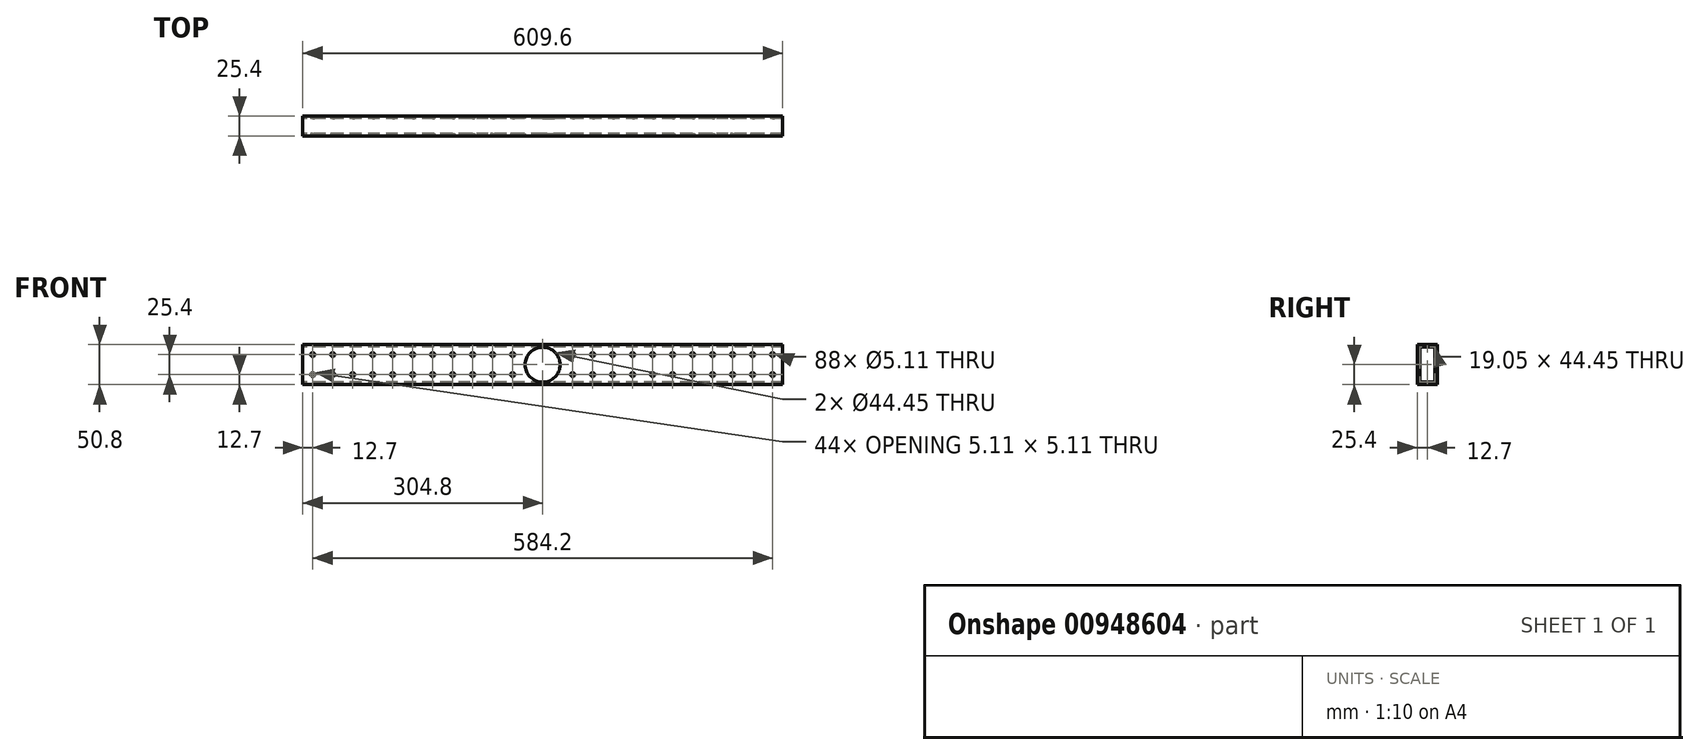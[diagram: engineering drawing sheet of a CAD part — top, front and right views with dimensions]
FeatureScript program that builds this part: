
annotation { "Feature Type Name" : "Feature", "Feature Type Description" : "" }
export const myFeature = defineFeature(function(context is Context, id is Id, definition is map)
    precondition{}
    {
        {
            var Q0;
            Q0=qCreatedBy(makeId("Right.planeOp"),FACE);
            var sketch = newSketch(context, id + "F0", { "sketchPlane" : qUnion([Q0])});
            skLineSegment(sketch, "E0.bottom", {"start": v(12.7, 25.4) * mm, "end": v(-12.7, 25.4) * mm});
            skLineSegment(sketch, "E0.top", {"start": v(12.7, -25.4) * mm, "end": v(-12.7, -25.4) * mm});
            skLineSegment(sketch, "E0.left", {"start": v(12.7, 25.4) * mm, "end": v(12.7, -25.4) * mm});
            skLineSegment(sketch, "E0.right", {"start": v(-12.7, 25.4) * mm, "end": v(-12.7, -25.4) * mm});
            skPoint(sketch, "E0.middle", {"position": v(0, 0) * mm});
            skLineSegment(sketch, "E1.0", {"start": v(9.53, 22.22) * mm, "end": v(-9.52, 22.22) * mm});
            skLineSegment(sketch, "E1.1", {"start": v(9.53, 22.22) * mm, "end": v(9.53, -22.23) * mm});
            skLineSegment(sketch, "E1.2", {"start": v(9.53, -22.23) * mm, "end": v(-9.52, -22.23) * mm});
            skLineSegment(sketch, "E1.3", {"start": v(-9.52, 22.22) * mm, "end": v(-9.53, -22.23) * mm});
            skSolve(sketch);
        }
        {
            var Q0;
            Q0 = qSketchRegion(id + "F0", true);
            extrude(context, id + "F1", {"entities" : qUnion([Q0]), "depth" : 609.6 * mm, "offsetDistance" : 25.4 * mm});
        }
        {
            var Q0;
            Q0=makeQuery(id+"F1.opExtrude","SWEPT_FACE",FACE,{"disambiguationData":[OSD([sQuery(id+"F0.wireOp",EDGE,"E0.right")])]});
            var sketch = newSketch(context, id + "F2", { "sketchPlane" : qUnion([Q0])});
            skCircle(sketch, "E2", {"center": v(12.7, 12.7) * mm, "radius": 2.55 * mm});
            skCircle(sketch, "E3.0.1.0", {"center": v(12.7, -12.7) * mm, "radius": 2.55 * mm});
            skCircle(sketch, "E3.1.0.0", {"center": v(38.1, 12.7) * mm, "radius": 2.55 * mm});
            skCircle(sketch, "E3.1.1.0", {"center": v(38.1, -12.7) * mm, "radius": 2.55 * mm});
            skCircle(sketch, "E3.2.0.0", {"center": v(63.5, 12.7) * mm, "radius": 2.55 * mm});
            skCircle(sketch, "E3.2.1.0", {"center": v(63.5, -12.7) * mm, "radius": 2.55 * mm});
            skCircle(sketch, "E3.3.0.0", {"center": v(88.9, 12.7) * mm, "radius": 2.55 * mm});
            skCircle(sketch, "E3.3.1.0", {"center": v(88.9, -12.7) * mm, "radius": 2.55 * mm});
            skCircle(sketch, "E3.4.0.0", {"center": v(114.3, 12.7) * mm, "radius": 2.55 * mm});
            skCircle(sketch, "E3.4.1.0", {"center": v(114.3, -12.7) * mm, "radius": 2.55 * mm});
            skCircle(sketch, "E3.5.0.0", {"center": v(139.7, 12.7) * mm, "radius": 2.55 * mm});
            skCircle(sketch, "E3.5.1.0", {"center": v(139.7, -12.7) * mm, "radius": 2.55 * mm});
            skCircle(sketch, "E3.6.0.0", {"center": v(165.1, 12.7) * mm, "radius": 2.55 * mm});
            skCircle(sketch, "E3.6.1.0", {"center": v(165.1, -12.7) * mm, "radius": 2.55 * mm});
            skCircle(sketch, "E3.7.0.0", {"center": v(190.5, 12.7) * mm, "radius": 2.55 * mm});
            skCircle(sketch, "E3.7.1.0", {"center": v(190.5, -12.7) * mm, "radius": 2.55 * mm});
            skCircle(sketch, "E3.8.0.0", {"center": v(215.9, 12.7) * mm, "radius": 2.55 * mm});
            skCircle(sketch, "E3.8.1.0", {"center": v(215.9, -12.7) * mm, "radius": 2.55 * mm});
            skCircle(sketch, "E3.9.0.0", {"center": v(241.3, 12.7) * mm, "radius": 2.55 * mm});
            skCircle(sketch, "E3.9.1.0", {"center": v(241.3, -12.7) * mm, "radius": 2.55 * mm});
            skCircle(sketch, "E3.10.0.0", {"center": v(266.7, 12.7) * mm, "radius": 2.55 * mm});
            skCircle(sketch, "E3.10.1.0", {"center": v(266.7, -12.7) * mm, "radius": 2.55 * mm});
            skCircle(sketch, "E3.11.0.0", {"center": v(292.1, 12.7) * mm, "radius": 2.55 * mm});
            skCircle(sketch, "E3.11.1.0", {"center": v(292.1, -12.7) * mm, "radius": 2.55 * mm});
            skCircle(sketch, "E3.12.0.0", {"center": v(317.5, 12.7) * mm, "radius": 2.55 * mm});
            skCircle(sketch, "E3.12.1.0", {"center": v(317.5, -12.7) * mm, "radius": 2.55 * mm});
            skCircle(sketch, "E3.13.0.0", {"center": v(342.9, 12.7) * mm, "radius": 2.55 * mm});
            skCircle(sketch, "E3.13.1.0", {"center": v(342.9, -12.7) * mm, "radius": 2.55 * mm});
            skCircle(sketch, "E3.14.0.0", {"center": v(368.3, 12.7) * mm, "radius": 2.55 * mm});
            skCircle(sketch, "E3.14.1.0", {"center": v(368.3, -12.7) * mm, "radius": 2.55 * mm});
            skCircle(sketch, "E3.15.0.0", {"center": v(393.7, 12.7) * mm, "radius": 2.55 * mm});
            skCircle(sketch, "E3.15.1.0", {"center": v(393.7, -12.7) * mm, "radius": 2.55 * mm});
            skCircle(sketch, "E3.16.0.0", {"center": v(419.1, 12.7) * mm, "radius": 2.55 * mm});
            skCircle(sketch, "E3.16.1.0", {"center": v(419.1, -12.7) * mm, "radius": 2.55 * mm});
            skCircle(sketch, "E3.17.0.0", {"center": v(444.5, 12.7) * mm, "radius": 2.55 * mm});
            skCircle(sketch, "E3.17.1.0", {"center": v(444.5, -12.7) * mm, "radius": 2.55 * mm});
            skCircle(sketch, "E3.18.0.0", {"center": v(469.9, 12.7) * mm, "radius": 2.55 * mm});
            skCircle(sketch, "E3.18.1.0", {"center": v(469.9, -12.7) * mm, "radius": 2.55 * mm});
            skCircle(sketch, "E3.19.0.0", {"center": v(495.3, 12.7) * mm, "radius": 2.55 * mm});
            skCircle(sketch, "E3.19.1.0", {"center": v(495.3, -12.7) * mm, "radius": 2.55 * mm});
            skCircle(sketch, "E3.20.0.0", {"center": v(520.7, 12.7) * mm, "radius": 2.55 * mm});
            skCircle(sketch, "E3.20.1.0", {"center": v(520.7, -12.7) * mm, "radius": 2.55 * mm});
            skCircle(sketch, "E3.21.0.0", {"center": v(546.1, 12.7) * mm, "radius": 2.55 * mm});
            skCircle(sketch, "E3.21.1.0", {"center": v(546.1, -12.7) * mm, "radius": 2.55 * mm});
            skCircle(sketch, "E3.22.0.0", {"center": v(571.5, 12.7) * mm, "radius": 2.55 * mm});
            skCircle(sketch, "E3.22.1.0", {"center": v(571.5, -12.7) * mm, "radius": 2.55 * mm});
            skCircle(sketch, "E3.23.0.0", {"center": v(596.9, 12.7) * mm, "radius": 2.55 * mm});
            skCircle(sketch, "E3.23.1.0", {"center": v(596.9, -12.7) * mm, "radius": 2.55 * mm});
            skLineSegment(sketch, "E3.direction1", {"start": v(12.7, 12.7) * mm, "end": v(38.1, 12.7) * mm, "construction": true});
            skLineSegment(sketch, "E3.direction2", {"start": v(12.7, 12.7) * mm, "end": v(12.7, -12.7) * mm, "construction": true});
            skSolve(sketch);
        }
        {
            var Q0;
            Q0 = qSketchRegion(id + "F2", true);
            extrude(context, id + "F3", {"entities" : qUnion([Q0]), "operationType" : NewBodyOperationType.REMOVE, "oppositeDirection" : true, "depth" : 25.4 * mm, "offsetDistance" : 25.4 * mm});
        }
        {
            var Q0;
            Q0=makeQuery(id+"F1.opExtrude","SWEPT_FACE",FACE,{"disambiguationData":[OSD([sQuery(id+"F0.wireOp",EDGE,"E0.right")])]});
            var sketch = newSketch(context, id + "F4", { "sketchPlane" : qUnion([Q0])});
            skCircle(sketch, "E4", {"center": v(304.8, 0) * mm, "radius": 22.23 * mm});
            skPoint(sketch, "E4.centerSnap0", {"position": v(304.8, 25.4) * mm});
            skSolve(sketch);
        }
        {
            var Q0;
            Q0 = qSketchRegion(id + "F4", true);
            extrude(context, id + "F5", {"entities" : qUnion([Q0]), "operationType" : NewBodyOperationType.REMOVE, "oppositeDirection" : true, "depth" : 25.4 * mm, "offsetDistance" : 25.4 * mm});
        }
    });
